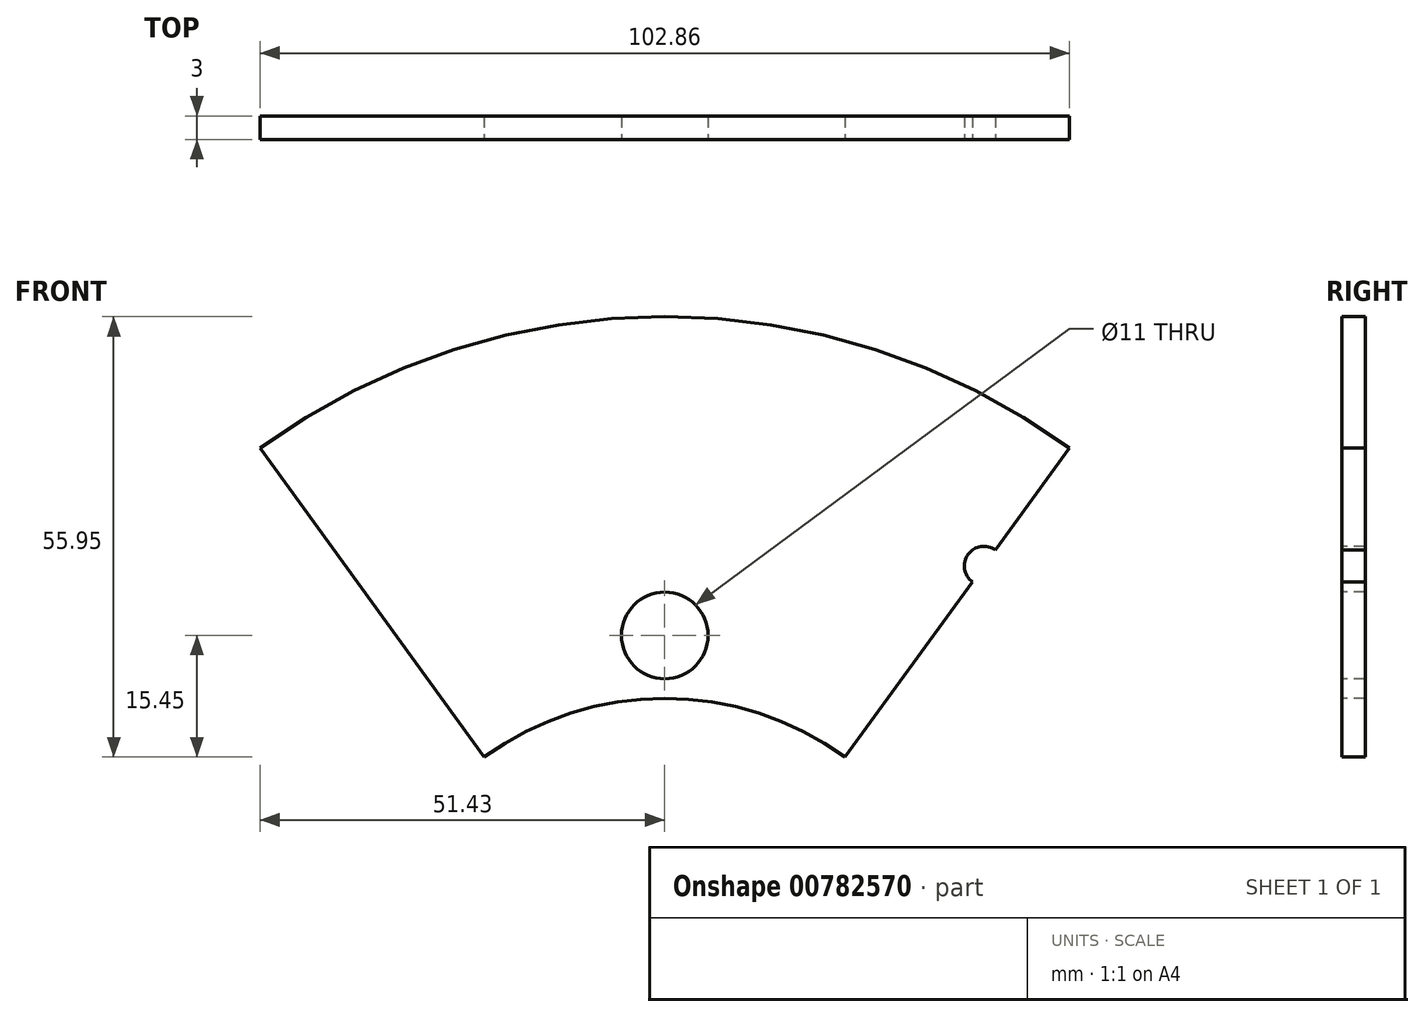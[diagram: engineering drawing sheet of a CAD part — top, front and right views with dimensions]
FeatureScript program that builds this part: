
annotation { "Feature Type Name" : "Feature", "Feature Type Description" : "" }
export const myFeature = defineFeature(function(context is Context, id is Id, definition is map)
    precondition{}
    {
        {
            var Q0;
            Q0=qCreatedBy(makeId("Front.planeOp"),FACE);
            var sketch = newSketch(context, id + "F0", { "sketchPlane" : qUnion([Q0])});
            skArc(sketch, "E0", {"start": v(51.43, 70.79) * mm, "mid": v(0, 87.5) * mm, "end": v(-51.43, 70.79) * mm});
            skLineSegment(sketch, "E1", {"start": v(0, 0) * mm, "end": v(51.43, 70.79) * mm});
            skLineSegment(sketch, "E2", {"start": v(0, 100.37) * mm, "end": v(0, -124.72) * mm, "construction": true});
            skLineSegment(sketch, "E3", {"start": v(-135.2, 0) * mm, "end": v(177.76, 0) * mm, "construction": true});
            skLineSegment(sketch, "E4.MirrorCS", {"start": v(0, 0) * mm, "end": v(-51.43, 70.79) * mm});
            skSolve(sketch);
        }
        {
            var Q0;
            Q0=makeQuery(id+"F0.imprint","IMPRINT",FACE,{"disambiguationData":[TD([[makeQuery(id+"F0.imprint","IMPRINT",EDGE,{"derivedFrom":sQuery(id+"F0.wireOp",EDGE,"E0")}),1.0]])]});
            extrude(context, id + "F1", {"entities" : qUnion([Q0]), "endBound" : BoundingType.SYMMETRIC, "depth" : 3 * mm, "offsetDistance" : 25 * mm});
        }
        {
            var Q0;
            Q0=makeQuery(id+"F1.opExtrude","CAP_FACE",FACE,{"disambiguationData":[OSD([sQuery(id+"F0.wireOp",EDGE,"E0"),sQuery(id+"F0.wireOp",EDGE,"E1"),sQuery(id+"F0.wireOp",EDGE,"E4.MirrorCS")])],"isStart":false});
            var sketch = newSketch(context, id + "F2", { "sketchPlane" : qUnion([Q0])});
            skLineSegment(sketch, "E5", {"start": v(0, 0) * mm, "end": v(0, 47) * mm});
            skCircle(sketch, "E6", {"center": v(0, 47) * mm, "radius": 5.5 * mm});
            skSolve(sketch);
        }
        {
            var Q0;
            Q0=makeQuery(id+"F2.imprint","IMPRINT",FACE,{"disambiguationData":[TD([[makeQuery(id+"F2.imprint","IMPRINT",EDGE,{"derivedFrom":sQuery(id+"F2.wireOp",EDGE,"E6")}),1.0]])]});
            extrude(context, id + "F3", {"entities" : qUnion([Q0]), "operationType" : NewBodyOperationType.REMOVE, "endBound" : BoundingType.THROUGH_ALL, "oppositeDirection" : true, "depth" : 25 * mm, "offsetDistance" : 25 * mm});
        }
        {
            var Q0;
            Q0=makeQuery(id+"F1.opExtrude","CAP_FACE",FACE,{"disambiguationData":[OSD([sQuery(id+"F0.wireOp",EDGE,"E0"),sQuery(id+"F0.wireOp",EDGE,"E1"),sQuery(id+"F0.wireOp",EDGE,"E4.MirrorCS")])],"isStart":false});
            var sketch = newSketch(context, id + "F4", { "sketchPlane" : qUnion([Q0])});
            skLineSegment(sketch, "E7", {"start": v(0, 0) * mm, "end": v(40.56, 55.82) * mm});
            skCircle(sketch, "E8", {"center": v(40.56, 55.82) * mm, "radius": 2.5 * mm});
            skSolve(sketch);
        }
        {
            var Q0;
            {var subQ0=sQuery(id+"F4.wireOp",EDGE,"E7");var subQ1=makeQuery(id+"F1.opExtrude","CAP_EDGE",EDGE,{"disambiguationData":[OSD([sQuery(id+"F0.wireOp",EDGE,"E1")])],"isStart":false});var subQ2=makeQuery(id+"F4.imprint","INTERSECT",VERTEX,{"derivedFrom":[subQ1,subQ0]});Q0=makeQuery(id+"F4.imprint","IMPRINT",FACE,{"disambiguationData":[TD([[makeQuery(id+"F4.imprint","IMPRINT",EDGE,{"disambiguationData":[TD([[subQ2,1.0]])],"derivedFrom":subQ0}),1.0]])]});}
            extrude(context, id + "F5", {"entities" : qUnion([Q0]), "operationType" : NewBodyOperationType.REMOVE, "endBound" : BoundingType.THROUGH_ALL, "oppositeDirection" : true, "depth" : 25 * mm, "offsetDistance" : 25 * mm});
        }
        {
            var Q0;
            Q0=makeQuery(id+"F1.opExtrude","CAP_FACE",FACE,{"disambiguationData":[OSD([sQuery(id+"F0.wireOp",EDGE,"E0"),sQuery(id+"F0.wireOp",EDGE,"E1"),sQuery(id+"F0.wireOp",EDGE,"E4.MirrorCS")])],"isStart":false});
            var sketch = newSketch(context, id + "F6", { "sketchPlane" : qUnion([Q0])});
            skCircle(sketch, "E9", {"center": v(0, 0) * mm, "radius": 39 * mm});
            skSolve(sketch);
        }
        {
            var Q0;
            Q0 = qSketchRegion(id + "F6", true);
            var Q1;
            {var subQ0=sQuery(id+"F6.wireOp",EDGE,"E9");var subQ1=sQuery(id+"F0.wireOp",EDGE,"E4.MirrorCS");var subQ2=makeQuery(id+"F1.opExtrude","CAP_EDGE",EDGE,{"disambiguationData":[OSD([subQ1])],"isStart":false});var subQ3=makeQuery(id+"F6.imprint","INTERSECT",VERTEX,{"derivedFrom":[subQ2,subQ0]});Q1=makeQuery(id+"F6.imprint","IMPRINT",FACE,{"disambiguationData":[TD([[makeQuery(id+"F6.imprint","IMPRINT",EDGE,{"disambiguationData":[TD([[subQ3,1.0]])],"derivedFrom":subQ0}),1.0]])]});}
            extrude(context, id + "F7", {"entities" : qUnion([Q0, Q1]), "operationType" : NewBodyOperationType.REMOVE, "endBound" : BoundingType.THROUGH_ALL, "oppositeDirection" : true, "depth" : 25 * mm, "offsetDistance" : 25 * mm});
        }
    });
